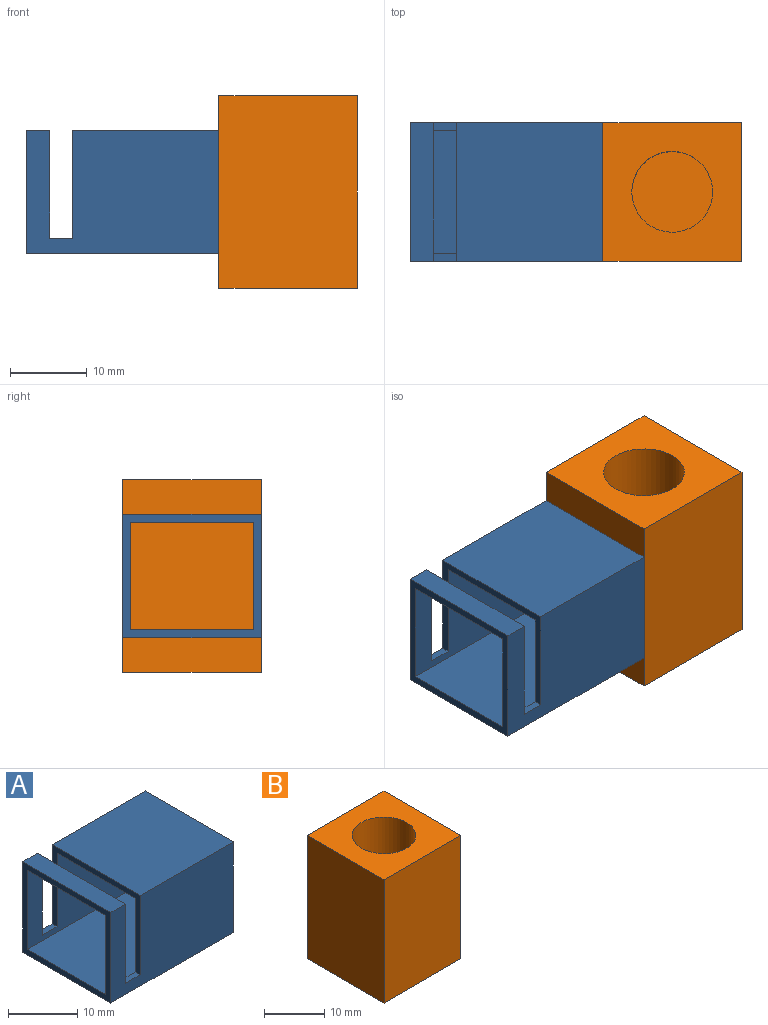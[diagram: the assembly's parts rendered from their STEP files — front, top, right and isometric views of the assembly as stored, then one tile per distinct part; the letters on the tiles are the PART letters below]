
ASSEMBLY  parts=2 mates=1
PART A: 16 faces, bbox 25x18x16 mm
  f0: plane 19x18mm, normal (0,0,1), area 342mm2, adj f1,f3,f10,f14
  f1: plane 25x16mm, normal (0,1,0), area 358mm2, adj f0,f4,f9,f10,f11,f12,f13,f14
  f2: plane 19x16mm, normal (0,0,-1), area 304mm2, adj f6,f8,f10,f14
  f3: plane 25x16mm, normal (0,-1,0), area 358mm2, adj f0,f4,f9,f10,f11,f13,f14,f15
  f4: plane 25x18mm, normal (0,0,-1), area 450mm2, adj f1,f3,f10,f11
  f5: plane 25x16mm, normal (0,0,1), area 400mm2, adj f6,f8,f10,f11
  f6: plane 25x14mm, normal (0,1,0), area 311mm2, adj f2,f5,f7,f10,f11,f13,f14,f15
  f7: plane 16x3mm, normal (0,0,-1), area 48mm2, adj f6,f8,f11,f13
  f8: plane 25x14mm, normal (0,-1,0), area 311mm2, adj f2,f5,f7,f10,f11,f12,f13,f14
  f9: plane 18x3mm, normal (0,0,1), area 54mm2, adj f1,f3,f11,f13
  f10: plane 18x16mm, normal (1,0,0), area 64mm2, adj f0,f1,f2,f3,f4,f5,f6,f8
  f11: plane 18x16mm, normal (-1,0,0), area 64mm2, adj f1,f3,f4,f5,f6,f7,f8,f9
  f12: plane 3x1mm, normal (0,0,1), area 3mm2, adj f1,f8,f13,f14
  f13: plane 18x14mm, normal (1,0,0), area 44mm2, adj f1,f3,f6,f7,f8,f9,f12,f15
  f14: plane 18x14mm, normal (-1,0,0), area 44mm2, adj f0,f1,f2,f3,f6,f8,f12,f15
  f15: plane 3x1mm, normal (0,0,1), area 3mm2, adj f3,f6,f13,f14
PART B: 8 faces, bbox 18x18x25 mm
  f0: plane 25x18mm, normal (1,0,0), area 450mm2, adj f1,f3,f4,f5
  f1: plane 25x18mm, normal (0,1,0), area 450mm2, adj f0,f2,f4,f5
  f2: plane 25x18mm, normal (-1,0,0), area 450mm2, adj f1,f3,f4,f5
  f3: plane 25x18mm, normal (0,-1,0), area 450mm2, adj f0,f2,f4,f5
  f4: plane 18x18mm, normal (0,0,1), area 237.4mm2, adj f0,f1,f2,f3,f6
  f5: plane 18x18mm, normal (0,0,-1), area 324mm2, adj f0,f1,f2,f3
  f6: cylinder r=5.25mm len=20mm, axis (0,0,1), area 659.7mm2, adj f4,f7
  f7: plane 10.5x10.5mm, normal (0,0,1), area 86.6mm2, adj f6
PLACE A t=(-5.5,0,0)mm
PLACE B t=(16,0,0)mm
MATE fastened B.f2 <-> A.f10  axis (-1,0,0) through (7,0,0)mm
